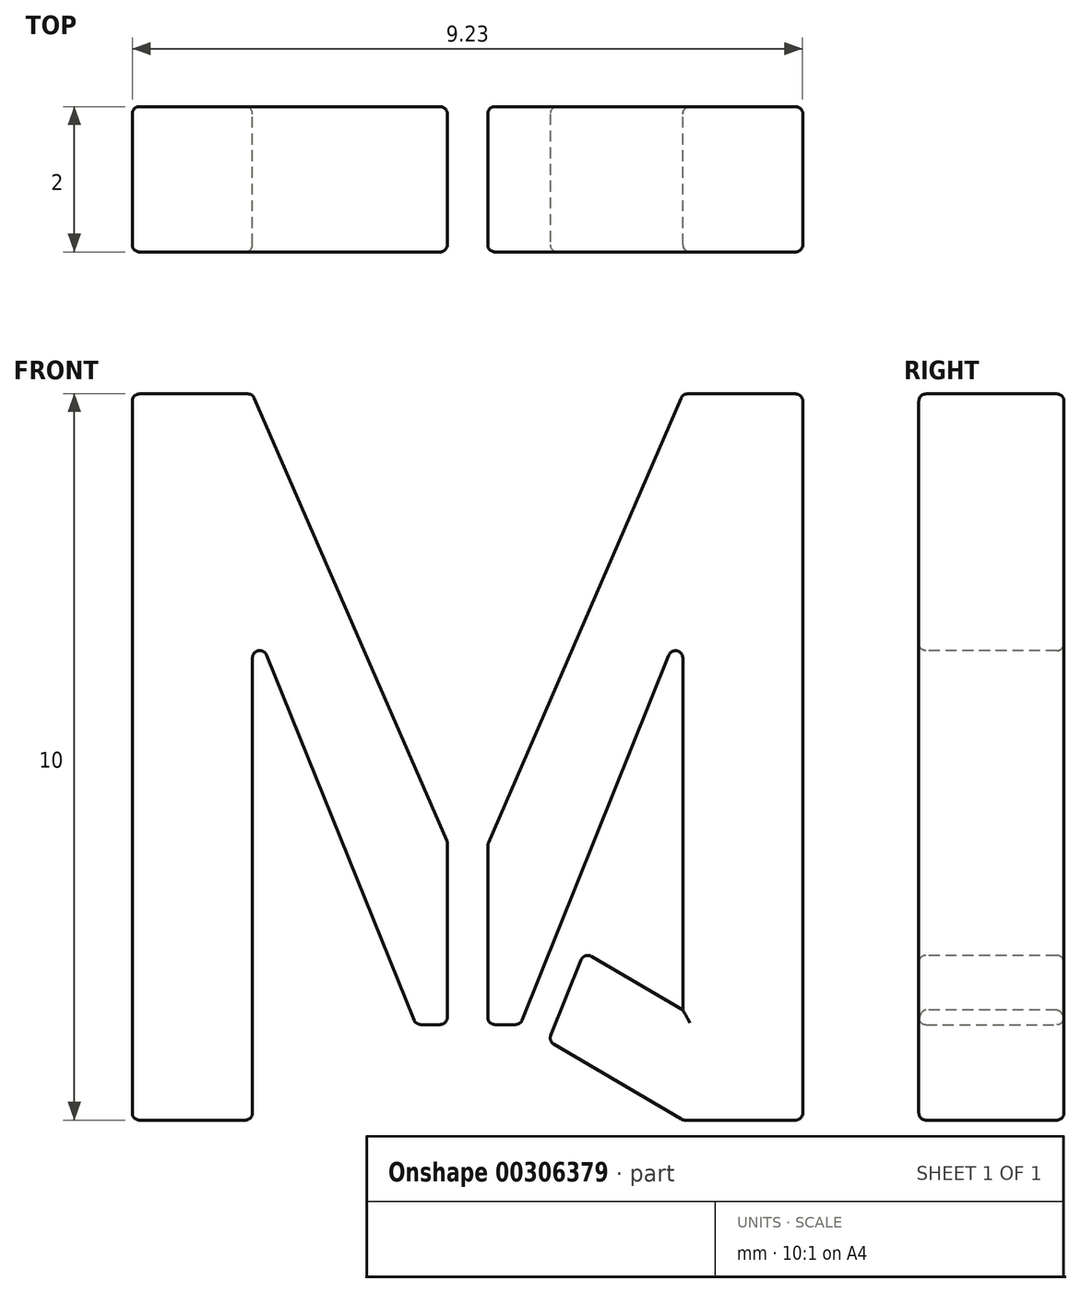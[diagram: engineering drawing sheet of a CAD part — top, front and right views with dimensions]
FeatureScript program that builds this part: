
annotation { "Feature Type Name" : "Feature", "Feature Type Description" : "" }
export const myFeature = defineFeature(function(context is Context, id is Id, definition is map)
    precondition{}
    {
        {
            var Q0;
            Q0=qCreatedBy(makeId("Front.planeOp"),FACE);
            var sketch = newSketch(context, id + "F0", { "sketchPlane" : qUnion([Q0])});
            skText(sketch, "E0", { "text": "M", "fontName": "AllertaStencil-Regular.ttf"});
            const initialGuessF0  = {"E0": [0, 0, 1, 0, 0.01]};
            skSetInitialGuess(sketch, initialGuessF0);
            skSolve(sketch);
        }
        {
            var Q0;
            Q0=makeQuery(id+"F0.imprint","IMPRINT",FACE,{"disambiguationData":[TD([[makeQuery(id+"F0.imprint","IMPRINT",EDGE,{"derivedFrom":sQuery(id+"F0.wireOp",EDGE,"E0.sketch_text.stroke-0")}),-1.0]])]});
            var Q1;
            Q1=makeQuery(id+"F0.imprint","IMPRINT",FACE,{"disambiguationData":[TD([[makeQuery(id+"F0.imprint","IMPRINT",EDGE,{"derivedFrom":sQuery(id+"F0.wireOp",EDGE,"E0.sketch_text.stroke-8")}),-1.0]])]});
            extrude(context, id + "F1", {"entities" : qUnion([Q0, Q1]), "depth" : 2 * mm});
        }
        {
            var Q0;
            Q0=makeQuery(id+"F1.opExtrude","CAP_FACE",FACE,{"disambiguationData":[OSD([sQuery(id+"F0.wireOp",EDGE,"E0.sketch_text.stroke-8"),sQuery(id+"F0.wireOp",EDGE,"E0.sketch_text.stroke-9"),sQuery(id+"F0.wireOp",EDGE,"E0.sketch_text.stroke-10"),sQuery(id+"F0.wireOp",EDGE,"E0.sketch_text.stroke-11"),sQuery(id+"F0.wireOp",EDGE,"E0.sketch_text.stroke-12"),sQuery(id+"F0.wireOp",EDGE,"E0.sketch_text.stroke-13"),sQuery(id+"F0.wireOp",EDGE,"E0.sketch_text.stroke-14"),sQuery(id+"F0.wireOp",EDGE,"E0.sketch_text.stroke-15")])],"isStart":false});
            var sketch = newSketch(context, id + "F2", { "sketchPlane" : qUnion([Q0])});
            skLineSegment(sketch, "E1", {"start": v(8.83, 0) * mm, "end": v(6.98, 1.09) * mm});
            skLineSegment(sketch, "E2", {"start": v(6.98, 1.09) * mm, "end": v(7.47, 2.31) * mm});
            skLineSegment(sketch, "E3", {"start": v(7.47, 2.31) * mm, "end": v(8.83, 1.51) * mm});
            skLineSegment(sketch, "E4", {"start": v(8.83, 1.51) * mm, "end": v(8.83, 0) * mm});
            skLineSegment(sketch, "E5", {"start": v(6.6, 1.32) * mm, "end": v(6.98, 1.09) * mm, "construction": true});
            skLineSegment(sketch, "E6", {"start": v(7.71, 4.1) * mm, "end": v(6.49, 4.59) * mm, "construction": true});
            skSolve(sketch);
        }
        {
            var Q0;
            Q0=makeQuery(id+"F2.imprint","IMPRINT",FACE,{"disambiguationData":[TD([[makeQuery(id+"F2.imprint","IMPRINT",EDGE,{"derivedFrom":sQuery(id+"F2.wireOp",EDGE,"E1")}),-1.0]])]});
            var Q1;
            Q1=makeQuery(id+"F1.opExtrude","CAP_FACE",FACE,{"disambiguationData":[OSD([sQuery(id+"F0.wireOp",EDGE,"E0.sketch_text.stroke-8"),sQuery(id+"F0.wireOp",EDGE,"E0.sketch_text.stroke-9"),sQuery(id+"F0.wireOp",EDGE,"E0.sketch_text.stroke-10"),sQuery(id+"F0.wireOp",EDGE,"E0.sketch_text.stroke-11"),sQuery(id+"F0.wireOp",EDGE,"E0.sketch_text.stroke-12"),sQuery(id+"F0.wireOp",EDGE,"E0.sketch_text.stroke-13"),sQuery(id+"F0.wireOp",EDGE,"E0.sketch_text.stroke-14"),sQuery(id+"F0.wireOp",EDGE,"E0.sketch_text.stroke-15")])],"isStart":true});
            extrude(context, id + "F3", {"entities" : qUnion([Q0]), "operationType" : NewBodyOperationType.ADD, "endBound" : BoundingType.UP_TO_SURFACE, "oppositeDirection" : true, "endBoundEntityFace" : qUnion([Q1]), "depth" : 25 * mm});
        }
        {
            var Q0;
            Q0=makeQuery(id+"F1.opExtrude","SWEPT_EDGE",EDGE,{"disambiguationData":[OSD([sQuery(id+"F0.wireOp",EDGE,"E0.sketch_text.stroke-6"),sQuery(id+"F0.wireOp",EDGE,"E0.sketch_text.stroke-7")])]});
            var Q1;
            Q1=makeQuery(id+"F1.opExtrude","SWEPT_EDGE",EDGE,{"disambiguationData":[OSD([sQuery(id+"F0.wireOp",EDGE,"E0.sketch_text.stroke-5"),sQuery(id+"F0.wireOp",EDGE,"E0.sketch_text.stroke-6")])]});
            var Q2;
            Q2=makeQuery(id+"F1.opExtrude","SWEPT_EDGE",EDGE,{"disambiguationData":[OSD([sQuery(id+"F0.wireOp",EDGE,"E0.sketch_text.stroke-4"),sQuery(id+"F0.wireOp",EDGE,"E0.sketch_text.stroke-5")])]});
            var Q3;
            Q3=makeQuery(id+"F1.opExtrude","SWEPT_EDGE",EDGE,{"disambiguationData":[OSD([sQuery(id+"F0.wireOp",EDGE,"E0.sketch_text.stroke-3"),sQuery(id+"F0.wireOp",EDGE,"E0.sketch_text.stroke-4")])]});
            var Q4;
            Q4=makeQuery(id+"F1.opExtrude","SWEPT_EDGE",EDGE,{"disambiguationData":[OSD([sQuery(id+"F0.wireOp",EDGE,"E0.sketch_text.stroke-2"),sQuery(id+"F0.wireOp",EDGE,"E0.sketch_text.stroke-3")])]});
            var Q5;
            Q5=makeQuery(id+"F1.opExtrude","SWEPT_EDGE",EDGE,{"disambiguationData":[OSD([sQuery(id+"F0.wireOp",EDGE,"E0.sketch_text.stroke-1"),sQuery(id+"F0.wireOp",EDGE,"E0.sketch_text.stroke-2")])]});
            var Q6;
            Q6=makeQuery(id+"F1.opExtrude","SWEPT_EDGE",EDGE,{"disambiguationData":[OSD([sQuery(id+"F0.wireOp",EDGE,"E0.sketch_text.stroke-0"),sQuery(id+"F0.wireOp",EDGE,"E0.sketch_text.stroke-1")])]});
            var Q7;
            Q7=makeQuery(id+"F1.opExtrude","SWEPT_EDGE",EDGE,{"disambiguationData":[OSD([sQuery(id+"F0.wireOp",EDGE,"E0.sketch_text.stroke-0"),sQuery(id+"F0.wireOp",EDGE,"E0.sketch_text.stroke-7")])]});
            var Q8;
            Q8=makeQuery(id+"F1.opExtrude","SWEPT_EDGE",EDGE,{"disambiguationData":[OSD([sQuery(id+"F0.wireOp",EDGE,"E0.sketch_text.stroke-13"),sQuery(id+"F0.wireOp",EDGE,"E0.sketch_text.stroke-14")])]});
            var Q9;
            Q9=makeQuery(id+"F1.opExtrude","SWEPT_EDGE",EDGE,{"disambiguationData":[OSD([sQuery(id+"F0.wireOp",EDGE,"E0.sketch_text.stroke-14"),sQuery(id+"F0.wireOp",EDGE,"E0.sketch_text.stroke-15")])]});
            var Q10;
            Q10=makeQuery(id+"F1.opExtrude","SWEPT_EDGE",EDGE,{"disambiguationData":[OSD([sQuery(id+"F0.wireOp",EDGE,"E0.sketch_text.stroke-8"),sQuery(id+"F0.wireOp",EDGE,"E0.sketch_text.stroke-15")])]});
            var Q11;
            Q11=makeQuery(id+"F1.opExtrude","SWEPT_EDGE",EDGE,{"disambiguationData":[OSD([sQuery(id+"F0.wireOp",EDGE,"E0.sketch_text.stroke-8"),sQuery(id+"F0.wireOp",EDGE,"E0.sketch_text.stroke-9")])]});
            var Q12;
            Q12=makeQuery(id+"F1.opExtrude","SWEPT_EDGE",EDGE,{"disambiguationData":[OSD([sQuery(id+"F0.wireOp",EDGE,"E0.sketch_text.stroke-11"),sQuery(id+"F0.wireOp",EDGE,"E0.sketch_text.stroke-12")])]});
            var Q13;
            Q13=makeQuery(id+"F1.opExtrude","SWEPT_EDGE",EDGE,{"disambiguationData":[OSD([sQuery(id+"F0.wireOp",EDGE,"E0.sketch_text.stroke-12"),sQuery(id+"F0.wireOp",EDGE,"E0.sketch_text.stroke-13")])]});
            var Q14;
            Q14=makeQuery(id+"F3.opExtrude","SWEPT_EDGE",EDGE,{"disambiguationData":[OSD([sQuery(id+"F2.wireOp",EDGE,"E1"),sQuery(id+"F2.wireOp",EDGE,"E2")])]});
            var Q15;
            {var subQ0=sQuery(id+"F0.wireOp",EDGE,"E0.sketch_text.stroke-10");Q15=makeQuery(id+"F3.boolean.opBoolean","MERGE",EDGE,{"derivedFrom":[makeQuery(id+"F1.opExtrude","SWEPT_EDGE",EDGE,{"disambiguationData":[OSD([subQ0,sQuery(id+"F0.wireOp",EDGE,"E0.sketch_text.stroke-11")])]}),makeQuery(id+"F3.opExtrude","SWEPT_EDGE",EDGE,{"disambiguationData":[OSD([subQ0,sQuery(id+"F2.wireOp",EDGE,"E1"),sQuery(id+"F2.wireOp",EDGE,"E4")])]})]});}
            var Q16;
            Q16=makeQuery(id+"F1.opExtrude","SWEPT_EDGE",EDGE,{"disambiguationData":[OSD([sQuery(id+"F0.wireOp",EDGE,"E0.sketch_text.stroke-9"),sQuery(id+"F0.wireOp",EDGE,"E0.sketch_text.stroke-10")])]});
            var Q17;
            Q17=makeQuery(id+"F3.opExtrude","SWEPT_EDGE",EDGE,{"disambiguationData":[OSD([sQuery(id+"F2.wireOp",EDGE,"E2"),sQuery(id+"F2.wireOp",EDGE,"E3")])]});
            var Q18;
            Q18=makeQuery(id+"F3.opExtrude","SWEPT_EDGE",EDGE,{"disambiguationData":[OSD([sQuery(id+"F0.wireOp",EDGE,"E0.sketch_text.stroke-11"),sQuery(id+"F2.wireOp",EDGE,"E3"),sQuery(id+"F2.wireOp",EDGE,"E4")])]});
            fillet(context, id + "F4", {"entities" : qUnion([Q0, Q1, Q2, Q3, Q4, Q5, Q6, Q7, Q8, Q9, Q10, Q11, Q12, Q13, Q14, Q15, Q16, Q17, Q18]), "radius" : .1 * mm, "tangentPropagation" : true, "allowEdgeOverflow" : false});
        }
        {
            var Q0;
            Q0=makeQuery(id+"F3.boolean.opBoolean","MERGE",FACE,{"derivedFrom":[makeQuery(id+"F1.opExtrude","CAP_FACE",FACE,{"disambiguationData":[OSD([sQuery(id+"F0.wireOp",EDGE,"E0.sketch_text.stroke-8"),sQuery(id+"F0.wireOp",EDGE,"E0.sketch_text.stroke-9"),sQuery(id+"F0.wireOp",EDGE,"E0.sketch_text.stroke-10"),sQuery(id+"F0.wireOp",EDGE,"E0.sketch_text.stroke-11"),sQuery(id+"F0.wireOp",EDGE,"E0.sketch_text.stroke-12"),sQuery(id+"F0.wireOp",EDGE,"E0.sketch_text.stroke-13"),sQuery(id+"F0.wireOp",EDGE,"E0.sketch_text.stroke-14"),sQuery(id+"F0.wireOp",EDGE,"E0.sketch_text.stroke-15")])],"isStart":false}),makeQuery(id+"F3.opExtrude","CAP_FACE",FACE,{"disambiguationData":[OSD([sQuery(id+"F2.wireOp",EDGE,"E1"),sQuery(id+"F2.wireOp",EDGE,"E2"),sQuery(id+"F2.wireOp",EDGE,"E3"),sQuery(id+"F2.wireOp",EDGE,"E4")])],"isStart":true})]});
            var Q1;
            Q1=makeQuery(id+"F1.opExtrude","CAP_FACE",FACE,{"disambiguationData":[OSD([sQuery(id+"F0.wireOp",EDGE,"E0.sketch_text.stroke-0"),sQuery(id+"F0.wireOp",EDGE,"E0.sketch_text.stroke-1"),sQuery(id+"F0.wireOp",EDGE,"E0.sketch_text.stroke-2"),sQuery(id+"F0.wireOp",EDGE,"E0.sketch_text.stroke-3"),sQuery(id+"F0.wireOp",EDGE,"E0.sketch_text.stroke-4"),sQuery(id+"F0.wireOp",EDGE,"E0.sketch_text.stroke-5"),sQuery(id+"F0.wireOp",EDGE,"E0.sketch_text.stroke-6"),sQuery(id+"F0.wireOp",EDGE,"E0.sketch_text.stroke-7")])],"isStart":false});
            var Q2;
            Q2=makeQuery(id+"F1.opExtrude","CAP_FACE",FACE,{"disambiguationData":[OSD([sQuery(id+"F0.wireOp",EDGE,"E0.sketch_text.stroke-0"),sQuery(id+"F0.wireOp",EDGE,"E0.sketch_text.stroke-1"),sQuery(id+"F0.wireOp",EDGE,"E0.sketch_text.stroke-2"),sQuery(id+"F0.wireOp",EDGE,"E0.sketch_text.stroke-3"),sQuery(id+"F0.wireOp",EDGE,"E0.sketch_text.stroke-4"),sQuery(id+"F0.wireOp",EDGE,"E0.sketch_text.stroke-5"),sQuery(id+"F0.wireOp",EDGE,"E0.sketch_text.stroke-6"),sQuery(id+"F0.wireOp",EDGE,"E0.sketch_text.stroke-7")])],"isStart":true});
            var Q3;
            {var subQ0=sQuery(id+"F0.wireOp",EDGE,"E0.sketch_text.stroke-15");var subQ1=sQuery(id+"F0.wireOp",EDGE,"E0.sketch_text.stroke-14");var subQ2=sQuery(id+"F0.wireOp",EDGE,"E0.sketch_text.stroke-13");var subQ3=sQuery(id+"F0.wireOp",EDGE,"E0.sketch_text.stroke-12");var subQ4=sQuery(id+"F0.wireOp",EDGE,"E0.sketch_text.stroke-11");var subQ5=sQuery(id+"F0.wireOp",EDGE,"E0.sketch_text.stroke-10");var subQ6=sQuery(id+"F0.wireOp",EDGE,"E0.sketch_text.stroke-9");var subQ7=sQuery(id+"F0.wireOp",EDGE,"E0.sketch_text.stroke-8");Q3=makeQuery(id+"F3.boolean.opBoolean","MERGE",FACE,{"derivedFrom":[makeQuery(id+"F1.opExtrude","CAP_FACE",FACE,{"disambiguationData":[OSD([subQ7,subQ6,subQ5,subQ4,subQ3,subQ2,subQ1,subQ0])],"isStart":true}),makeQuery(id+"F3.opExtrude","CAP_FACE",FACE,{"disambiguationData":[OSD([subQ7,subQ6,subQ5,subQ4,subQ3,subQ2,subQ1,subQ0])],"isStart":false})]});}
            fillet(context, id + "F5", {"entities" : qUnion([Q0, Q1, Q2, Q3]), "radius" : .1 * mm, "allowEdgeOverflow" : false});
        }
    });
